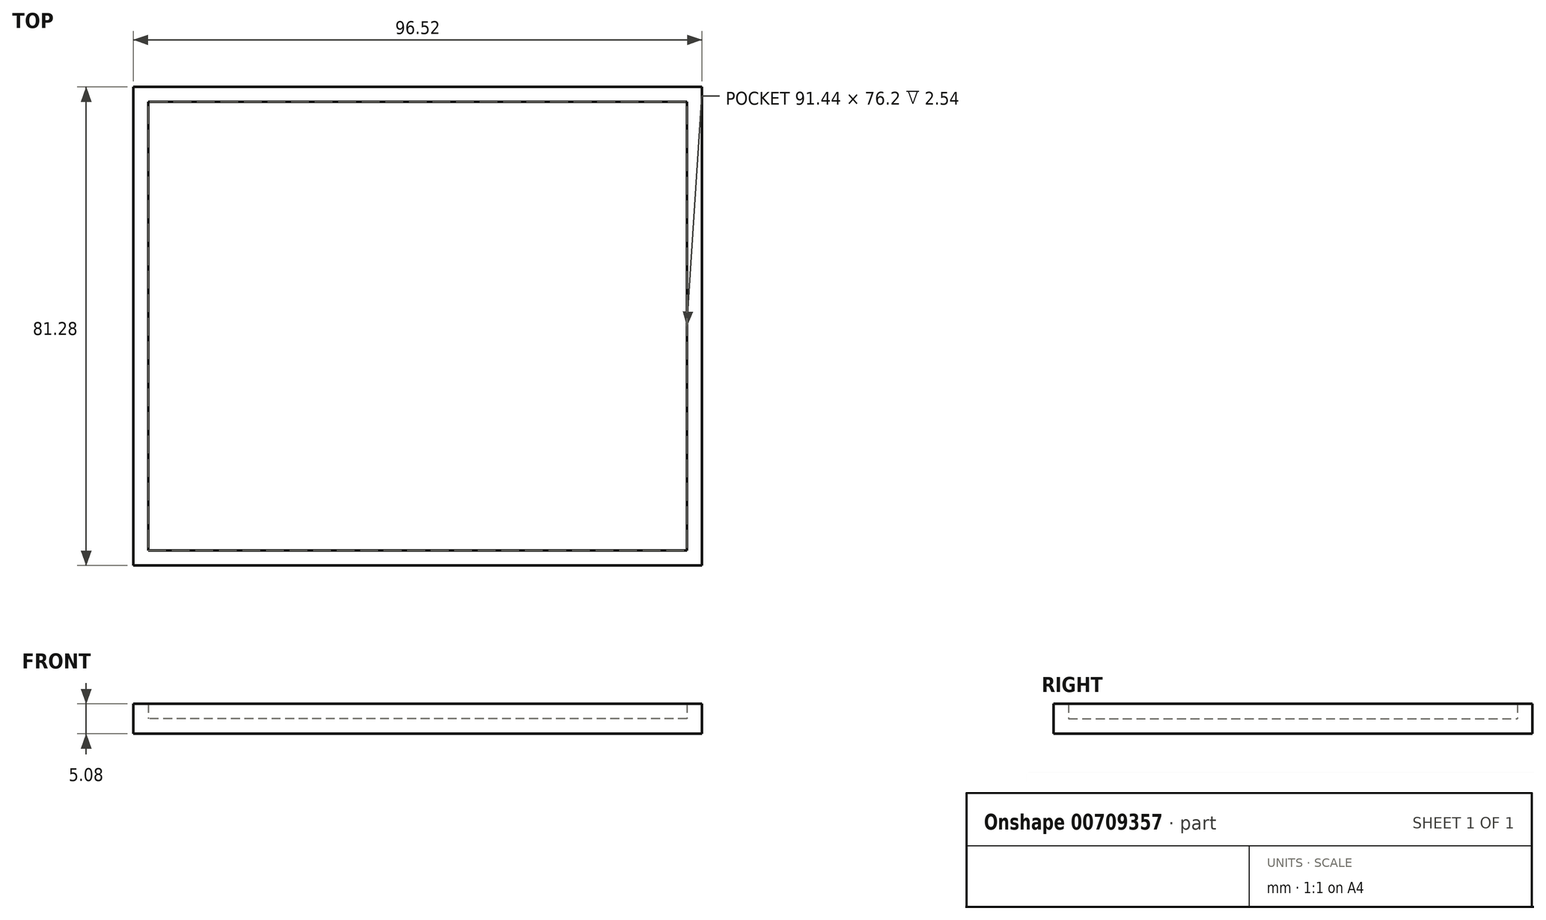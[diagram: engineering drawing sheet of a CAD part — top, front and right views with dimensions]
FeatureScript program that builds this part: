
annotation { "Feature Type Name" : "Feature", "Feature Type Description" : "" }
export const myFeature = defineFeature(function(context is Context, id is Id, definition is map)
    precondition{}
    {
        {
            var Q0;
            Q0=qCreatedBy(makeId("Front.planeOp"),FACE);
            var sketch = newSketch(context, id + "F0", { "sketchPlane" : qUnion([Q0])});
            skLineSegment(sketch, "E0.bottom", {"start": v(48.26, 2.54) * mm, "end": v(-48.26, 2.54) * mm});
            skLineSegment(sketch, "E0.top", {"start": v(48.26, -2.54) * mm, "end": v(-48.26, -2.54) * mm});
            skLineSegment(sketch, "E0.left", {"start": v(48.26, 2.54) * mm, "end": v(48.26, -2.54) * mm});
            skLineSegment(sketch, "E0.right", {"start": v(-48.26, 2.54) * mm, "end": v(-48.26, -2.54) * mm});
            skPoint(sketch, "E0.middle", {"position": v(0, 0) * mm});
            skSolve(sketch);
        }
        {
            var Q0;
            Q0=makeQuery(id+"F0.imprint","IMPRINT",FACE,{"disambiguationData":[TD([[makeQuery(id+"F0.imprint","IMPRINT",EDGE,{"derivedFrom":sQuery(id+"F0.wireOp",EDGE,"E0.bottom")}),1.0]])]});
            extrude(context, id + "F1", {"entities" : qUnion([Q0]), "endBound" : BoundingType.SYMMETRIC, "depth" : 81.28 * mm, "offsetDistance" : 25.4 * mm});
        }
        {
            var Q0;
            Q0=makeQuery(id+"F1.opExtrude","SWEPT_FACE",FACE,{"disambiguationData":[OSD([sQuery(id+"F0.wireOp",EDGE,"E0.bottom")])]});
            shell(context, id + "F2", {"entities" : qUnion([Q0]), "thickness" : 2.54 * mm});
        }
    });
